# Revit family: Franke_ChillandCup_CC05_EC-A600_MS_EC_A600_FM_EC_A800_FM_EC(USA)
name_source: partatom
category: Specialty Equipment
revit_build: Autodesk Revit 2015 (Build: 20140606_1530(x64)
units: mm (PartAtom-declared; Revit-internal decimal feet)

## types (1)
- ChillandCup CC05 EC-A600 MS EC,A600 FM EC,A800 FM EC(100-120V/USA)
    Assembly Code = Cup warmer, Milk cooler
    Cost = 0 $
    Cup warmer = up to 80 cups
    Cycle = 60 Hz
    Cycle Alternative = 0 Hz
    Depth (mm) = 489 mm  [stored 1.60433 ft]
    Description = Cup warmer for up to 80 cups, Milk cooler (5 liter)
    Energy loss acc. to DIN 18873 = 2.020 kWh/24 h - 230 V
    Height (mm) = 582 mm  [stored 1.90945 ft]
    Keynote = Cup warmer, Milk cooler
    Manufacturer = Franke
    Milk cooler = 5 l
    Model = ChillandCup CC05 EC-A600 MS EC,A600 FM EC, A800 FM EC
    Number of Nutral Conductors = 1
    Number of Poles = 1
    Number of Protective Conductors = 1
    Temperature range = + 3° to + 8°
    URL = https://www.franke.com
    Volts max. = 120 V
    Volts min. = 100 V
    Watts = 190 W
    Weight = 29 kg
    Width (mm) = 320 mm  [stored 1.04987 ft]

note: [stored X ft] marks values corroborated as IEEE doubles in the binary element streams (Revit-internal decimal feet)

## geometry (parser evidence)
native form markers: Extrusion x1
no freeform markers — native parametric forms only
